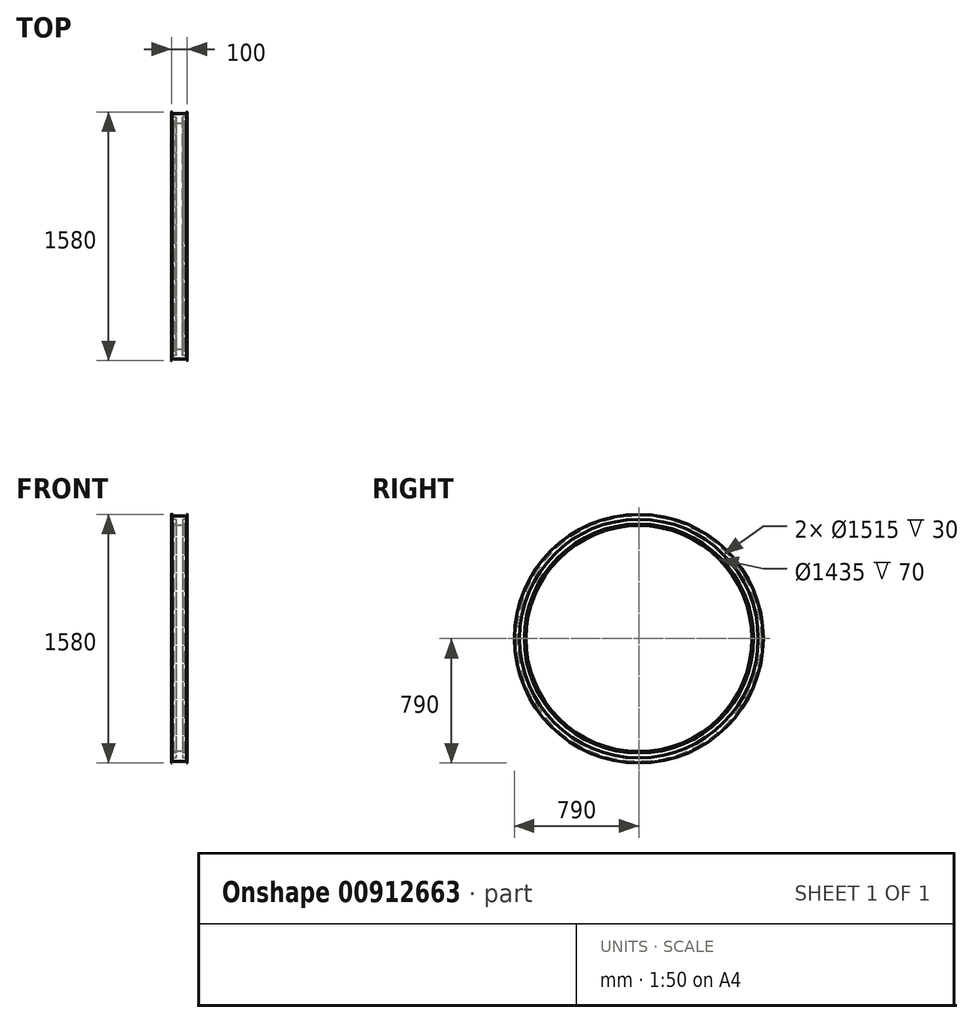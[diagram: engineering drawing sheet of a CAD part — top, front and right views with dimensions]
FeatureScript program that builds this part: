
annotation { "Feature Type Name" : "Feature", "Feature Type Description" : "" }
export const myFeature = defineFeature(function(context is Context, id is Id, definition is map)
    precondition{}
    {
        {
            var Q0;
            Q0=qCreatedBy(makeId("Front.planeOp"),FACE);
            var sketch = newSketch(context, id + "F0", { "sketchPlane" : qUnion([Q0])});
            skLineSegment(sketch, "E0", {"start": v(0, 0) * mm, "end": v(-35, 0) * mm});
            skLineSegment(sketch, "E1", {"start": v(-35, 0) * mm, "end": v(-35, 10) * mm});
            skLineSegment(sketch, "E2", {"start": v(-35, 10) * mm, "end": v(-20, 10) * mm});
            skLineSegment(sketch, "E3", {"start": v(-20, 10) * mm, "end": v(-20, 40) * mm});
            skLineSegment(sketch, "E4", {"start": v(-20, 40) * mm, "end": v(-50, 40) * mm});
            skLineSegment(sketch, "E5", {"start": v(-50, 40) * mm, "end": v(-50, 70) * mm});
            skLineSegment(sketch, "E6", {"start": v(-47.5, 72.5) * mm, "end": v(-45, 72.5) * mm});
            skLineSegment(sketch, "E7", {"start": v(-45, 72.5) * mm, "end": v(-45, 61) * mm});
            skLineSegment(sketch, "E8", {"start": v(-45, 61) * mm, "end": v(0, 61) * mm});
            skLineSegment(sketch, "E9", {"start": v(0, 61) * mm, "end": v(0, 0) * mm});
            skPoint(sketch, "E10.visualSharp", {"position": v(-50, 72.5) * mm});
            skArc(sketch, "E10.filletArc", {"start": v(-47.5, 72.5) * mm, "mid": v(-49.27, 71.77) * mm, "end": v(-50, 70) * mm});
            skLineSegment(sketch, "E11.MirrorCS", {"start": v(45, 61) * mm, "end": v(0, 61) * mm});
            skLineSegment(sketch, "E12.MirrorCS", {"start": v(45, 72.5) * mm, "end": v(45, 61) * mm});
            skLineSegment(sketch, "E13.MirrorCS", {"start": v(47.5, 72.5) * mm, "end": v(45, 72.5) * mm});
            skArc(sketch, "E14.MirrorCS", {"start": v(47.5, 72.5) * mm, "mid": v(49.27, 71.77) * mm, "end": v(50, 70) * mm});
            skLineSegment(sketch, "E15.MirrorCS", {"start": v(50, 40) * mm, "end": v(50, 70) * mm});
            skLineSegment(sketch, "E16.MirrorCS", {"start": v(20, 40) * mm, "end": v(50, 40) * mm});
            skLineSegment(sketch, "E17.MirrorCS", {"start": v(20, 10) * mm, "end": v(20, 40) * mm});
            skLineSegment(sketch, "E18.MirrorCS", {"start": v(35, 10) * mm, "end": v(20, 10) * mm});
            skLineSegment(sketch, "E19.MirrorCS", {"start": v(35, 0) * mm, "end": v(35, 10) * mm});
            skLineSegment(sketch, "E20.MirrorCS", {"start": v(0, 0) * mm, "end": v(35, 0) * mm});
            skLineSegment(sketch, "E21", {"start": v(0, 0) * mm, "end": v(0, -717.5) * mm, "construction": true});
            skLineSegment(sketch, "E22", {"start": v(-62.84, -717.5) * mm, "end": v(113.78, -717.5) * mm, "construction": true});
            skSolve(sketch);
        }
        {
            var Q0;
            Q0=makeQuery(id+"F0.imprint","IMPRINT",FACE,{"disambiguationData":[TD([[makeQuery(id+"F0.imprint","IMPRINT",EDGE,{"derivedFrom":sQuery(id+"F0.wireOp",EDGE,"E9")}),1.0]])]});
            var Q1;
            Q1=makeQuery(id+"F0.imprint","IMPRINT",FACE,{"disambiguationData":[TD([[makeQuery(id+"F0.imprint","IMPRINT",EDGE,{"derivedFrom":sQuery(id+"F0.wireOp",EDGE,"E0")}),-1.0]])]});
            var Q2;
            Q2=sQuery(id+"F0.wireOp",EDGE,"E22");
            revolve(context, id + "F1", {"surfaceOperationType" : NewSurfaceOperationType.NEW, "entities" : qUnion([Q0, Q1]), "axis" : qUnion([Q2]), "revolveType" : RevolveType.FULL});
        }
    });
